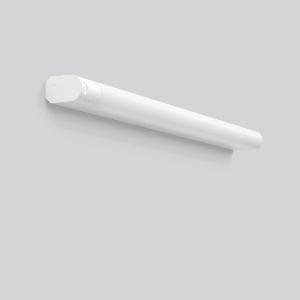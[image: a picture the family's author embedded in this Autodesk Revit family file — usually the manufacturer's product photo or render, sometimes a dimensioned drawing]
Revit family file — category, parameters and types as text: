
# Revit family: rt_44_451173_002_1_1285
name_source: partatom
category: Lighting Fixtures
units: mm (PartAtom-declared; Revit-internal decimal feet)

## family parameters
Cut with Voids When Loaded = No
Host = Face
Light Source = No
Part Type = Normal
Room Calculation Point = No
Round Connector Dimension = Use Diameter
Shared = No

## types (1)
- RT 44 (1 x LED Modul 840, 1500 lm, 4000)
    Apparent Load = 15 VA
    CIE Flux Codes = 36 65 85 81 100
    Color Rendering = 80
    Color Temperature = 4000
    Default Elevation = 1800 mm
    Description = Series: RT 44
Linear luminaire, can be used as wall and mirror luminaire. Base: aluminium, powder-coated. End caps: plastic (polycarbonate), shock-resistant. Diffuser: plastic (polycarbonate), opal. Suitable for Ceiling mounting, Wall (surface). Can be installed horizontally and vertically. Very easy installation thanks to Plug+Play connection. With Schukoplug socket. Driver integrated. High type of protection: IP44 for use in wet areas. 
Colour: pure white (RAL 9010)
Length: 977 mm
Width: 55 mm
Height: 87 mm
Lamp: LED
Socket: without socket
Colour temperature: 4000K
Colour rendering index (CRI): 80
System power: 15 W
Rated luminous flux: 1500 lm
Luminous efficiency: 100 lm/W
Control gear: Regulated power supply
Protection class: I
Type of protection: IP 44
    Height = 87 mm
    Lamp = 1 x LED Modul 840
    Lamp Light Flux = 1500 lm
    Lamp count = 1
    Length = 977 mm
    Lifetime = 50000 h
    Luminous efficacy = 100 lm/W
    Manufacturer = RZB
    ModVariant = No
    Model = 451173.002.1
    Mounting Place = Ceiling, Wall
    Mounting Type = Surface mounted
    Number of Poles = 1
    OnlyDefault = Yes
    Power Factor = 1
    Product Name = RT 44
    Product group = Surface mounted ceiling and wall luminaires
    ProductGroupID = 305
    Protection Class = Protection class I
    Protection Degree = IP 44
    RLX_Detail_Level = 1
    RLX_Emergency_Light_Flux = 0 lm
    RLX_Emergency_Type = 0
    RLX_Emergency_Type_DB = No
    RlxData = <blob elided: 27633 chars, md5=d4912a71>
    Socket = socket
    Standby Power = 0 W
    System Light Flux = 1500 lm
    System Power = 15 W
    Type Comments = Product without accessories
    Type Image = 451059.752.jpg
    URL = http://relux.com
    VarID = ---
    Voltage = 230 V
    Voltage Range = 220-240 V
    Weight = 0.00 kg
    Width = 55 mm

## geometry (parser evidence)
native form markers: Blend x4, Sweep x16
no freeform markers — native parametric forms only
